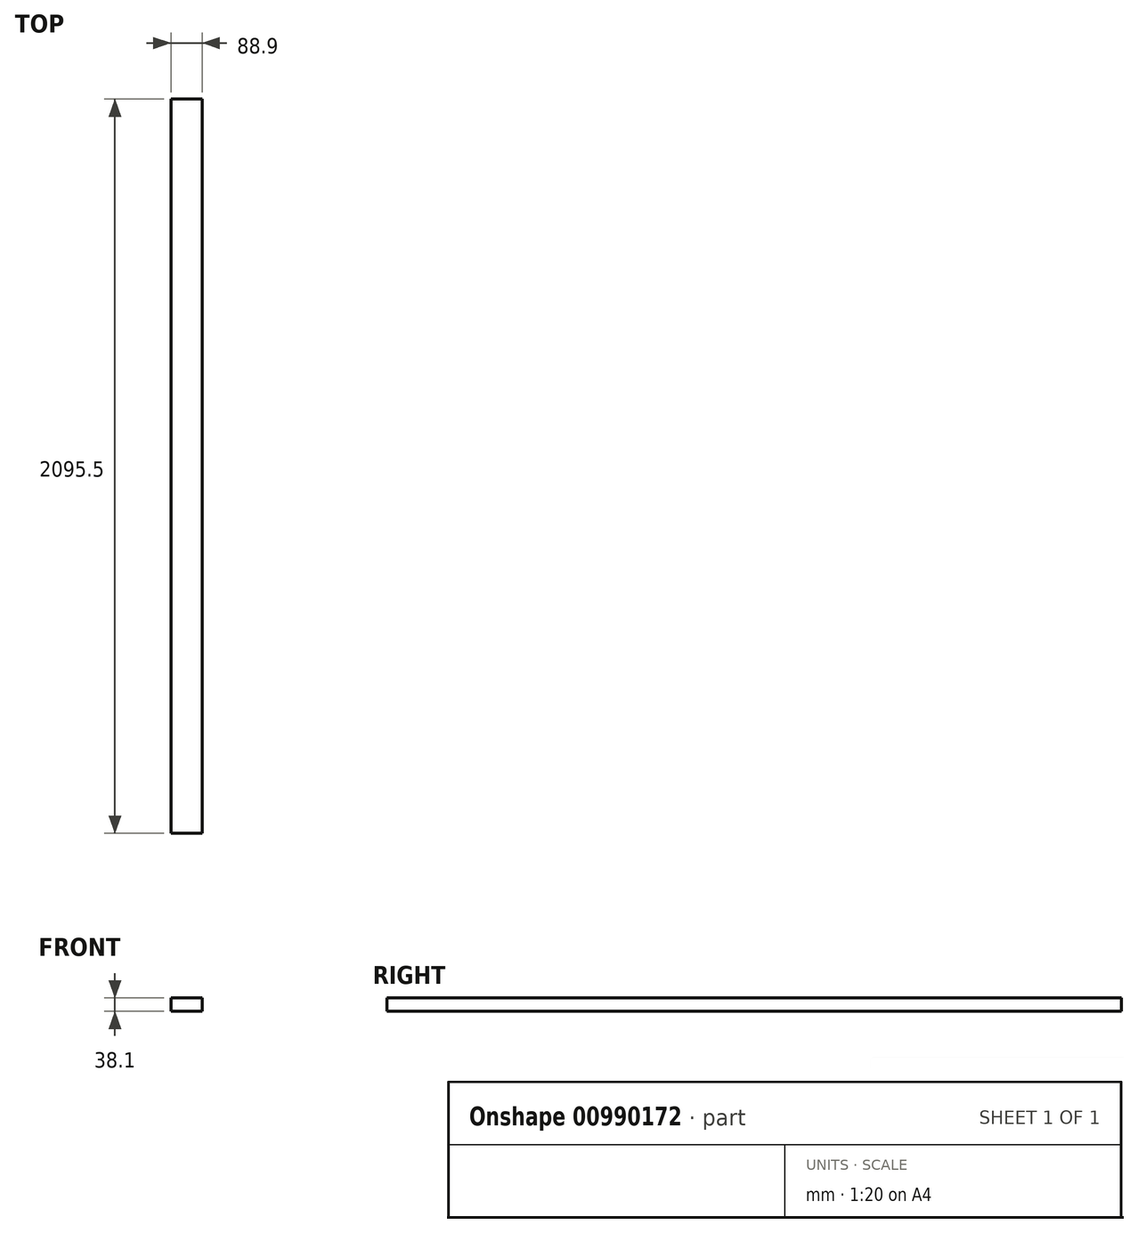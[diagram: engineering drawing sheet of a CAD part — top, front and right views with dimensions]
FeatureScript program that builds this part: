
annotation { "Feature Type Name" : "Feature", "Feature Type Description" : "" }
export const myFeature = defineFeature(function(context is Context, id is Id, definition is map)
    precondition{}
    {
        {
            assignVariable(context, id + "F0", {"name" : "w", "anyValue" : 38.1 * mm});
        }
        {
            var Q0;
            Q0=qCreatedBy(makeId("Top.planeOp"),FACE);
            var sketch = newSketch(context, id + "F1", { "sketchPlane" : qUnion([Q0])});
            skLineSegment(sketch, "E0.bottom", {"start": v(44.45, 1047.75) * mm, "end": v(-44.45, 1047.75) * mm});
            skLineSegment(sketch, "E0.top", {"start": v(44.45, -1047.75) * mm, "end": v(-44.45, -1047.75) * mm});
            skLineSegment(sketch, "E0.left", {"start": v(44.45, 1047.75) * mm, "end": v(44.45, -1047.75) * mm});
            skLineSegment(sketch, "E0.right", {"start": v(-44.45, 1047.75) * mm, "end": v(-44.45, -1047.75) * mm});
            skPoint(sketch, "E0.middle", {"position": v(0, 0) * mm});
            skSolve(sketch);
        }
        {
            var Q0;
            Q0=qSketchRegion(id+"F1",true);
            extrude(context, id + "F2", {"entities" : qUnion([Q0]), "depth" : getVariable(context, 'w'), "offsetDistance" : 25.4 * mm});
        }
    });
